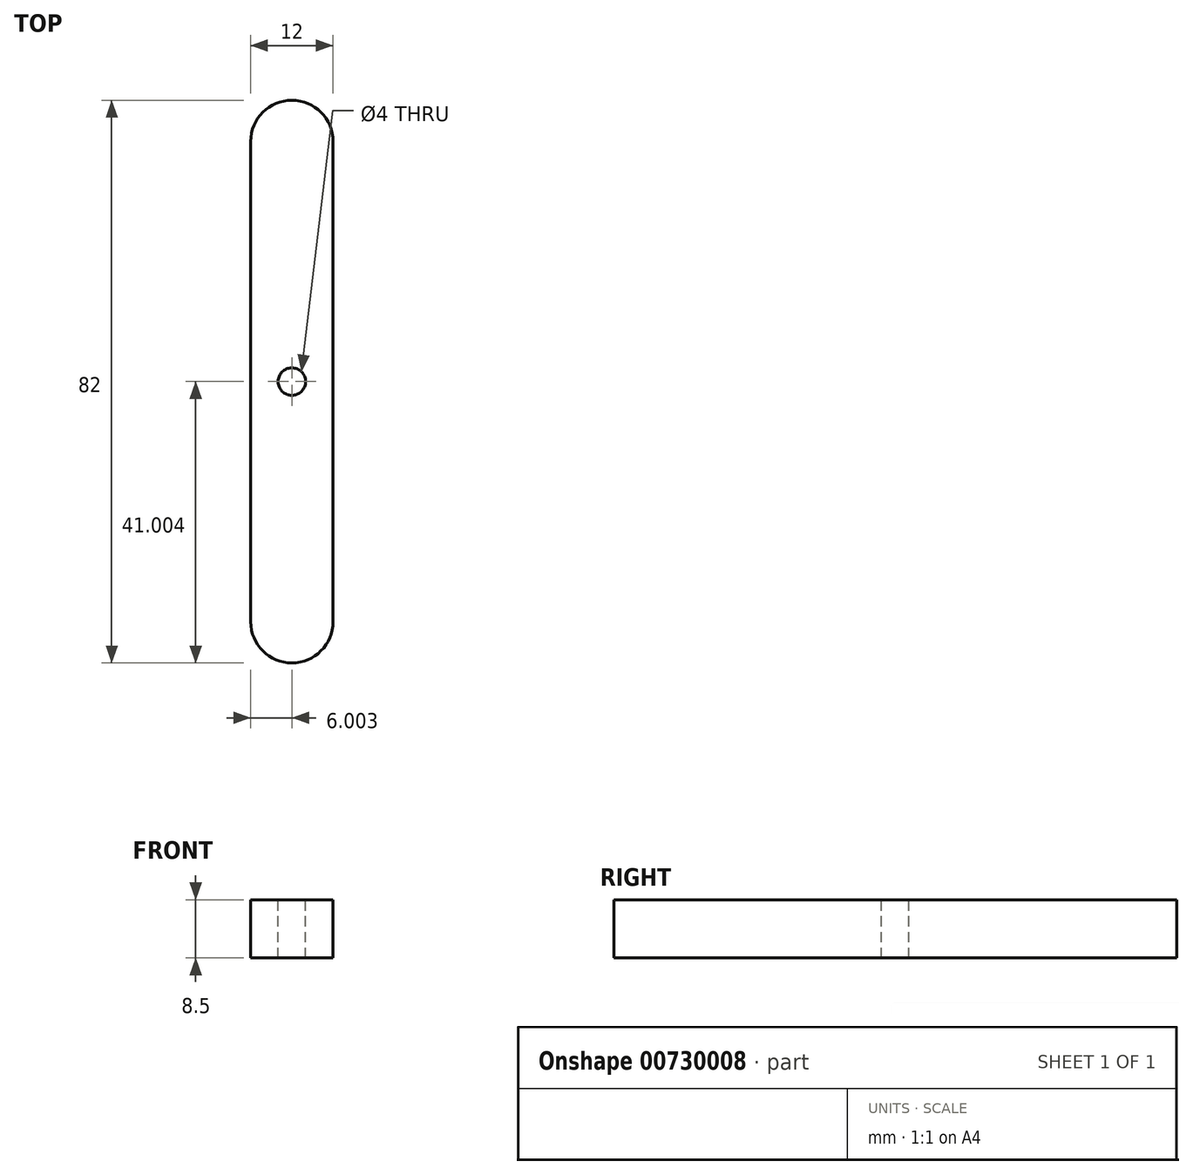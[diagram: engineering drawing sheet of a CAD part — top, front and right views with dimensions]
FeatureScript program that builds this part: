
annotation { "Feature Type Name" : "Feature", "Feature Type Description" : "" }
export const myFeature = defineFeature(function(context is Context, id is Id, definition is map)
    precondition{}
    {
        {
            var Q0;
            Q0=qCreatedBy(makeId("Top.planeOp"),FACE);
            var sketch = newSketch(context, id + "F0", { "sketchPlane" : qUnion([Q0])});
            skLineSegment(sketch, "E0", {"start": v(-56.5, 35.44) * mm, "end": v(-56.5, -34.56) * mm});
            skLineSegment(sketch, "E1", {"start": v(-44.5, 35.44) * mm, "end": v(-44.5, -34.56) * mm});
            skArc(sketch, "E2", {"start": v(-56.5, 35.44) * mm, "mid": v(-50.5, 41.44) * mm, "end": v(-44.5, 35.44) * mm});
            skArc(sketch, "E3", {"start": v(-56.5, -34.56) * mm, "mid": v(-50.5, -40.56) * mm, "end": v(-44.5, -34.56) * mm});
            skSolve(sketch);
        }
        {
            var Q0;
            Q0=makeQuery(id+"F0.imprint","IMPRINT",FACE,{"disambiguationData":[TD([[makeQuery(id+"F0.imprint","IMPRINT",EDGE,{"derivedFrom":sQuery(id+"F0.wireOp",EDGE,"E0")}),1.0]])]});
            extrude(context, id + "F1", {"entities" : qUnion([Q0]), "depth" : 8.5 * mm, "offsetDistance" : 25 * mm});
        }
        {
            var Q0;
            Q0=makeQuery(id+"F1.opExtrude","CAP_FACE",FACE,{"disambiguationData":[OSD([sQuery(id+"F0.wireOp",EDGE,"E0"),sQuery(id+"F0.wireOp",EDGE,"E1"),sQuery(id+"F0.wireOp",EDGE,"E2"),sQuery(id+"F0.wireOp",EDGE,"E3")])],"isStart":false});
            var sketch = newSketch(context, id + "F2", { "sketchPlane" : qUnion([Q0])});
            skCircle(sketch, "E4", {"center": v(-50.5, 0.44) * mm, "radius": 2 * mm});
            skSolve(sketch);
        }
        {
            var Q0;
            Q0=makeQuery(id+"F2.imprint","IMPRINT",FACE,{"disambiguationData":[TD([[makeQuery(id+"F2.imprint","IMPRINT",EDGE,{"derivedFrom":sQuery(id+"F2.wireOp",EDGE,"E4")}),1.0]])]});
            extrude(context, id + "F3", {"entities" : qUnion([Q0]), "operationType" : NewBodyOperationType.REMOVE, "oppositeDirection" : true, "depth" : 25 * mm, "offsetDistance" : 25 * mm});
        }
    });
